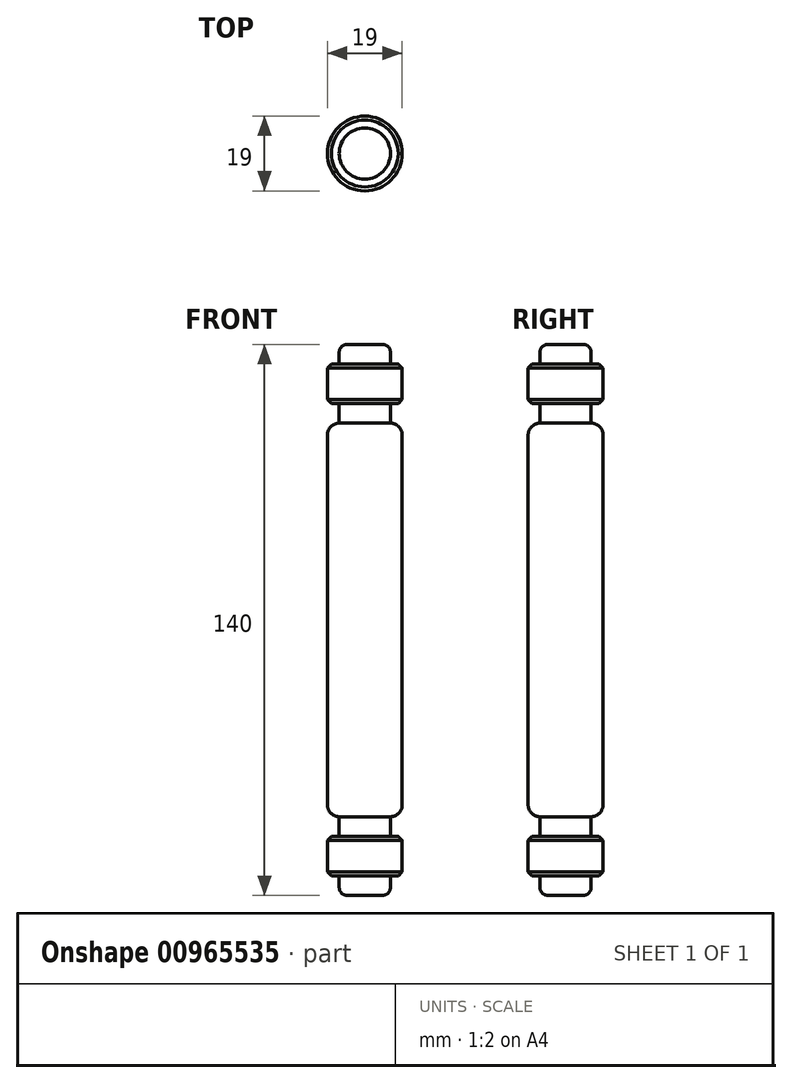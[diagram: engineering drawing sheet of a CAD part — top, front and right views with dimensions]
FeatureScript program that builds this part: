
annotation { "Feature Type Name" : "Feature", "Feature Type Description" : "" }
export const myFeature = defineFeature(function(context is Context, id is Id, definition is map)
    precondition{}
    {
        {
            var Q0;
            Q0=qCreatedBy(makeId("Front.planeOp"),FACE);
            var sketch = newSketch(context, id + "F0", { "sketchPlane" : qUnion([Q0])});
            skLineSegment(sketch, "E0", {"start": v(0, 0) * mm, "end": v(0, 70) * mm});
            skLineSegment(sketch, "E1", {"start": v(0, 0) * mm, "end": v(4.5, 0) * mm});
            skLineSegment(sketch, "E2", {"start": v(6.5, 2) * mm, "end": v(6.5, 5) * mm});
            skLineSegment(sketch, "E3", {"start": v(6.5, 5) * mm, "end": v(9.5, 5) * mm});
            skLineSegment(sketch, "E4", {"start": v(9.5, 5) * mm, "end": v(9.5, 15) * mm});
            skLineSegment(sketch, "E5", {"start": v(9.5, 15) * mm, "end": v(6.5, 15) * mm});
            skLineSegment(sketch, "E6", {"start": v(6.5, 15) * mm, "end": v(6.5, 20) * mm});
            skLineSegment(sketch, "E7", {"start": v(6.5, 20) * mm, "end": v(6.5, 20) * mm});
            skLineSegment(sketch, "E8", {"start": v(9.5, 23) * mm, "end": v(9.5, 70) * mm});
            skLineSegment(sketch, "E9", {"start": v(9.5, 70) * mm, "end": v(0, 70) * mm});
            skPoint(sketch, "E10.visualSharp", {"position": v(6.5, 0) * mm});
            skArc(sketch, "E10.filletArc", {"start": v(4.5, 0) * mm, "mid": v(5.91, 0.59) * mm, "end": v(6.5, 2) * mm});
            skPoint(sketch, "E11.visualSharp", {"position": v(9.5, 20) * mm});
            skArc(sketch, "E11.filletArc", {"start": v(6.5, 20) * mm, "mid": v(8.62, 20.88) * mm, "end": v(9.5, 23) * mm});
            skSolve(sketch);
        }
        {
            var Q0;
            Q0 = qSketchRegion(id + "F0", true);
            var Q1;
            Q1=sQuery(id+"F0.wireOp",EDGE,"E0");
            revolve(context, id + "F1", {"surfaceOperationType" : NewSurfaceOperationType.NEW, "entities" : qUnion([Q0]), "axis" : qUnion([Q1]), "revolveType" : RevolveType.FULL});
        }
        {
            var Q0;
            Q0=makeQuery(id+"F1.opRevolve","SWEPT_FACE",FACE,{"disambiguationData":[OSD([sQuery(id+"F0.wireOp",EDGE,"E9")])]});
            cPlane(context, id + "F2", {"entities" : qUnion([Q0]), "cplaneType" : CPlaneType.OFFSET, "offset" : 0 * mm, "width" : 150 * mm, "height" : 150 * mm});
        }
        {
            var Q0;
            Q0=makeQuery(id+"F1.opRevolve","SWEPT_BODY",BODY,{"disambiguationData":[OSD([sQuery(id+"F0.wireOp",EDGE,"E0"),sQuery(id+"F0.wireOp",EDGE,"E1"),sQuery(id+"F0.wireOp",EDGE,"E2"),sQuery(id+"F0.wireOp",EDGE,"E3"),sQuery(id+"F0.wireOp",EDGE,"E4"),sQuery(id+"F0.wireOp",EDGE,"E5"),sQuery(id+"F0.wireOp",EDGE,"E6"),sQuery(id+"F0.wireOp",EDGE,"E7"),sQuery(id+"F0.wireOp",EDGE,"E8"),sQuery(id+"F0.wireOp",EDGE,"E9")])]});
            var Q1;
            Q1=qCreatedBy(id+"F2.planeOp",FACE);
            mirror(context, id + "F3", {"operationType" : NewBodyOperationType.ADD, "entities" : qUnion([Q0]), "mirrorPlane" : qUnion([Q1])});
        }
        {
            var Q0;
            Q0=makeQuery(id+"F3.opPattern","COPY",FACE,{"derivedFrom":makeQuery(id+"F1.opRevolve","SWEPT_FACE",FACE,{"disambiguationData":[OSD([sQuery(id+"F0.wireOp",EDGE,"E4")])]}),"instanceName":"1"});
            var Q1;
            Q1=makeQuery(id+"F1.opRevolve","SWEPT_FACE",FACE,{"disambiguationData":[OSD([sQuery(id+"F0.wireOp",EDGE,"E4")])]});
            chamfer(context, id + "F4", {"entities" : qUnion([Q0, Q1]), "width" : 1 * mm, "tangentPropagation" : true});
        }
    });
